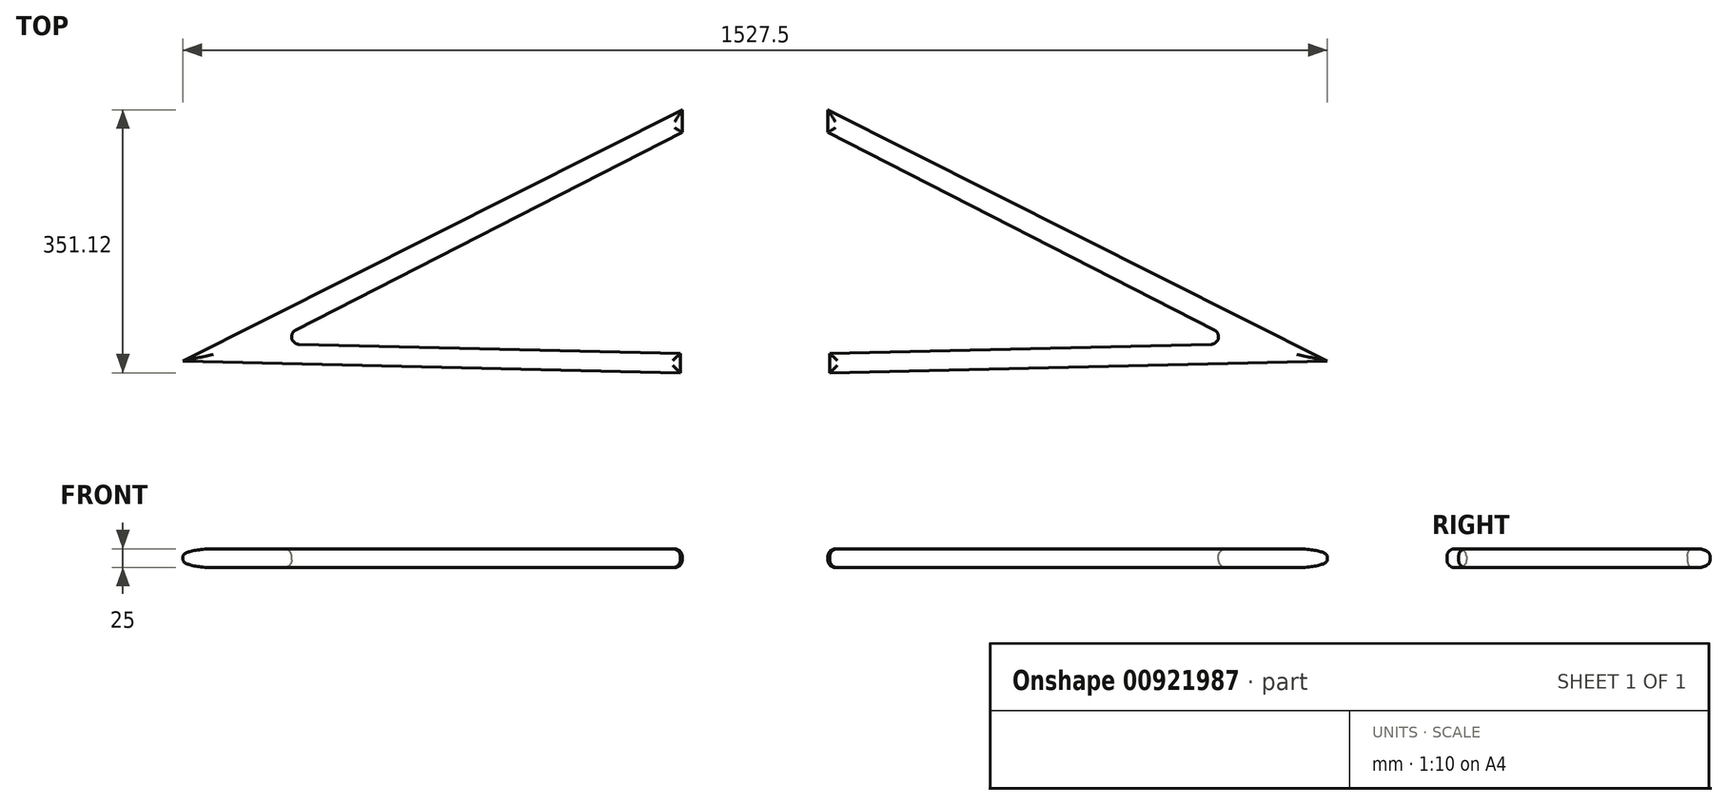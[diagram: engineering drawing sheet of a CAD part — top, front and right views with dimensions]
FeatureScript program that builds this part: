
annotation { "Feature Type Name" : "Feature", "Feature Type Description" : "" }
export const myFeature = defineFeature(function(context is Context, id is Id, definition is map)
    precondition{}
    {
        {
            var Q0;
            Q0=qCreatedBy(makeId("Top.planeOp"),FACE);
            var sketch = newSketch(context, id + "F0", { "sketchPlane" : qUnion([Q0])});
            skLineSegment(sketch, "E0", {"start": v(97.34, -863.5) * mm, "end": v(763.75, -1199.03) * mm});
            skLineSegment(sketch, "E1", {"start": v(763.75, -1199.03) * mm, "end": v(99.8, -1214.62) * mm});
            skLineSegment(sketch, "E2", {"start": v(97.34, -893.6) * mm, "end": v(648.3, -1175.66) * mm});
            skLineSegment(sketch, "E3", {"start": v(648.3, -1175.66) * mm, "end": v(99.8, -1188.73) * mm});
            skLineSegment(sketch, "E4", {"start": v(99.8, -1188.73) * mm, "end": v(99.8, -1214.62) * mm});
            skLineSegment(sketch, "E5", {"start": v(97.34, -893.6) * mm, "end": v(97.34, -863.5) * mm});
            skSolve(sketch);
        }
        {
            var Q0;
            Q0=makeQuery(id+"F0.imprint","IMPRINT",FACE,{"disambiguationData":[TD([[makeQuery(id+"F0.imprint","IMPRINT",EDGE,{"derivedFrom":sQuery(id+"F0.wireOp",EDGE,"E0")}),-1.0]])]});
            extrude(context, id + "F1", {"entities" : qUnion([Q0]), "depth" : 25 * mm, "offsetDistance" : 25 * mm});
        }
        {
            var Q0;
            Q0=makeQuery(id+"F1.opExtrude","CAP_FACE",FACE,{"disambiguationData":[OSD([sQuery(id+"F0.wireOp",EDGE,"E0"),sQuery(id+"F0.wireOp",EDGE,"E1"),sQuery(id+"F0.wireOp",EDGE,"E2"),sQuery(id+"F0.wireOp",EDGE,"E3"),sQuery(id+"F0.wireOp",EDGE,"E4"),sQuery(id+"F0.wireOp",EDGE,"E5")])],"isStart":false});
            var Q1;
            Q1=makeQuery(id+"F1.opExtrude","CAP_FACE",FACE,{"disambiguationData":[OSD([sQuery(id+"F0.wireOp",EDGE,"E0"),sQuery(id+"F0.wireOp",EDGE,"E1"),sQuery(id+"F0.wireOp",EDGE,"E2"),sQuery(id+"F0.wireOp",EDGE,"E3"),sQuery(id+"F0.wireOp",EDGE,"E4"),sQuery(id+"F0.wireOp",EDGE,"E5")])],"isStart":true});
            var Q2;
            Q2=makeQuery(id+"F1.opExtrude","SWEPT_EDGE",EDGE,{"disambiguationData":[OSD([sQuery(id+"F0.wireOp",EDGE,"E2"),sQuery(id+"F0.wireOp",EDGE,"E3")])]});
            fillet(context, id + "F2", {"entities" : qUnion([Q0, Q1, Q2]), "radius" : 10 * mm, "tangentPropagation" : true, "allowEdgeOverflow" : false});
        }
        {
            var Q0;
            Q0=makeQuery(id+"F1.opExtrude","SWEPT_BODY",BODY,{"disambiguationData":[OSD([sQuery(id+"F0.wireOp",EDGE,"E0"),sQuery(id+"F0.wireOp",EDGE,"E1"),sQuery(id+"F0.wireOp",EDGE,"E2"),sQuery(id+"F0.wireOp",EDGE,"E3"),sQuery(id+"F0.wireOp",EDGE,"E4"),sQuery(id+"F0.wireOp",EDGE,"E5")])]});
            var Q1;
            Q1=qCreatedBy(makeId("Right.planeOp"),FACE);
            mirror(context, id + "F3", {"entities" : qUnion([Q0]), "mirrorPlane" : qUnion([Q1])});
        }
    });
